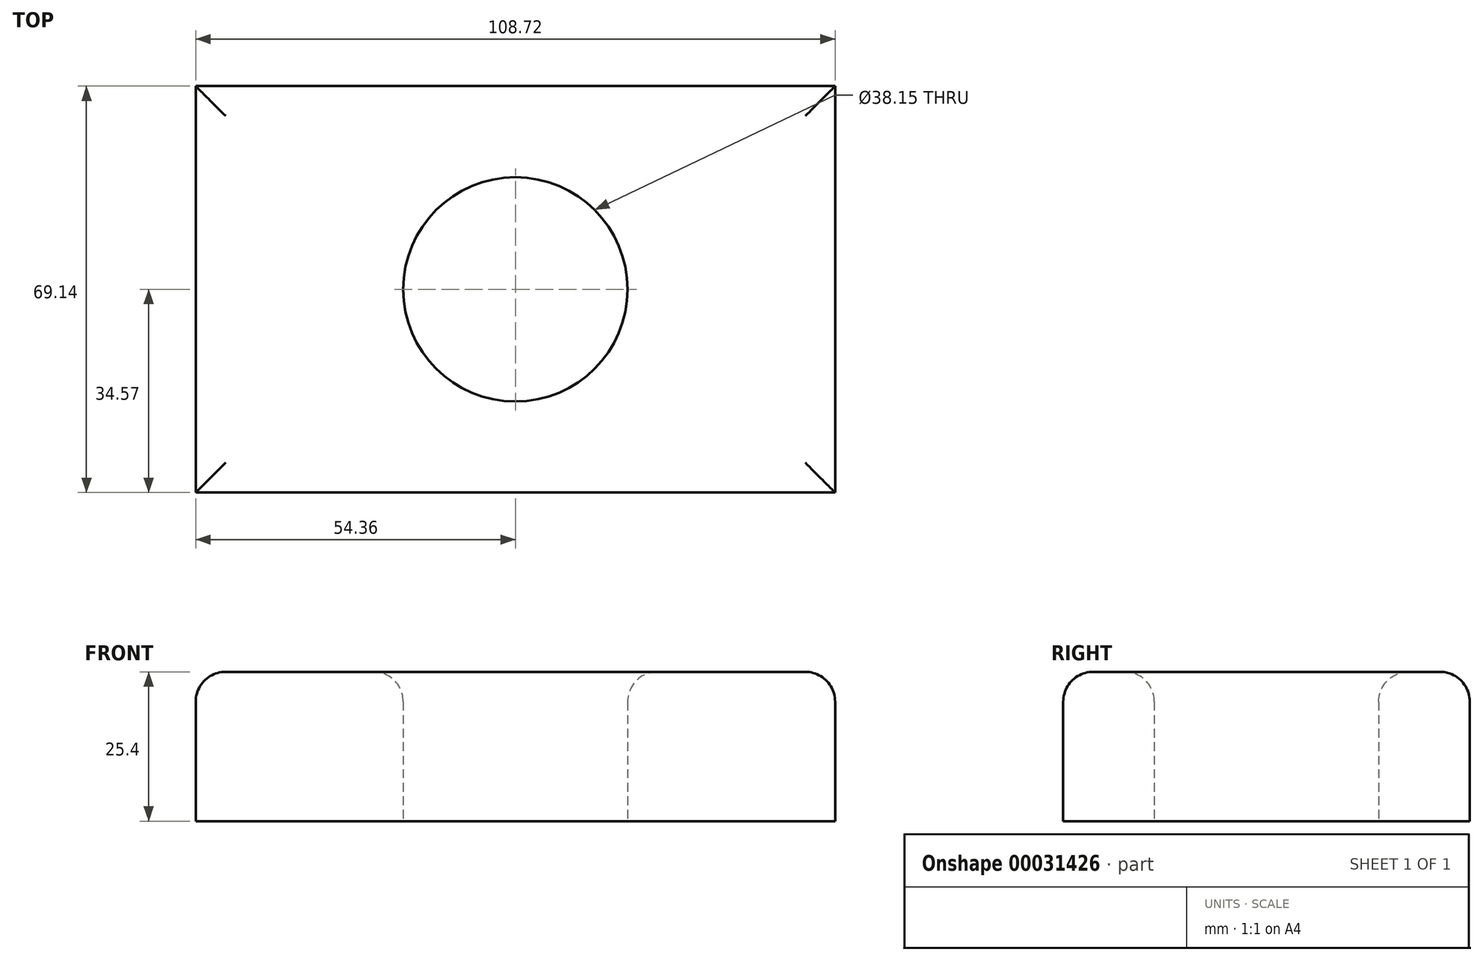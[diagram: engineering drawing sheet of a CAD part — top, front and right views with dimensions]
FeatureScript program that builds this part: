
annotation { "Feature Type Name" : "Feature", "Feature Type Description" : "" }
export const myFeature = defineFeature(function(context is Context, id is Id, definition is map)
    precondition{}
    {
        {
            var Q0;
            Q0=qCreatedBy(makeId("Top.planeOp"),FACE);
            var sketch = newSketch(context, id + "F0", { "sketchPlane" : qUnion([Q0])});
            skLineSegment(sketch, "E0.bottom", {"start": v(54.36, 34.57) * mm, "end": v(-54.36, 34.57) * mm});
            skLineSegment(sketch, "E0.top", {"start": v(54.36, -34.57) * mm, "end": v(-54.36, -34.57) * mm});
            skLineSegment(sketch, "E0.left", {"start": v(54.36, 34.57) * mm, "end": v(54.36, -34.57) * mm});
            skLineSegment(sketch, "E0.right", {"start": v(-54.36, 34.57) * mm, "end": v(-54.36, -34.57) * mm});
            skPoint(sketch, "E0.middle", {"position": v(0, 0) * mm});
            skCircle(sketch, "E1", {"center": v(0, 0) * mm, "radius": 19.08 * mm});
            skSolve(sketch);
        }
        {
            var Q0;
            Q0=makeQuery(id+"F0.imprint","IMPRINT",FACE,{"disambiguationData":[TD([[makeQuery(id+"F0.imprint","IMPRINT",EDGE,{"derivedFrom":sQuery(id+"F0.wireOp",EDGE,"E0.bottom")}),1.0]])]});
            extrude(context, id + "F1", {"entities" : qUnion([Q0]), "depth" : 25.4 * mm});
        }
        {
            var Q0;
            Q0=makeQuery(id+"F1.opExtrude","CAP_EDGE",EDGE,{"disambiguationData":[OSD([sQuery(id+"F0.wireOp",EDGE,"E0.top")])],"isStart":false});
            var Q1;
            Q1=makeQuery(id+"F1.opExtrude","CAP_EDGE",EDGE,{"disambiguationData":[OSD([sQuery(id+"F0.wireOp",EDGE,"E0.right")])],"isStart":false});
            var Q2;
            Q2=makeQuery(id+"F1.opExtrude","CAP_EDGE",EDGE,{"disambiguationData":[OSD([sQuery(id+"F0.wireOp",EDGE,"E0.bottom")])],"isStart":false});
            var Q3;
            Q3=makeQuery(id+"F1.opExtrude","CAP_EDGE",EDGE,{"disambiguationData":[OSD([sQuery(id+"F0.wireOp",EDGE,"E0.left")])],"isStart":false});
            var Q4;
            Q4=makeQuery(id+"F1.opExtrude","CAP_EDGE",EDGE,{"disambiguationData":[OSD([sQuery(id+"F0.wireOp",EDGE,"E1")])],"isStart":false});
            fillet(context, id + "F2", {"entities" : qUnion([Q0, Q1, Q2, Q3, Q4]), "radius" : 5.08 * mm, "tangentPropagation" : true, "allowEdgeOverflow" : false});
        }
    });
